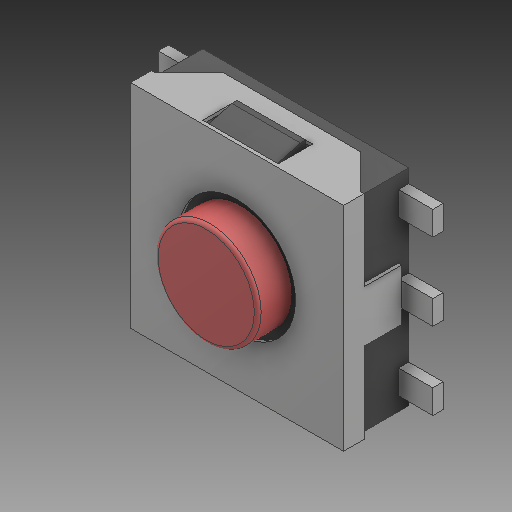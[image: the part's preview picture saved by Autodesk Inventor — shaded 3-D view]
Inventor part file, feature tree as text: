
AUTODESK INVENTOR PART (.ipt)
format: ipt  version: 2020 (Build 240168000, 168)  size: 180,224 bytes
history: native  units: mm
features: other x1, fillet x1
ambient origin geometry x8: Origin, YZ Plane, XZ Plane, XY Plane, X Axis, Y Axis, Z Axis, Center Point
bodies: Body1 (feature_tree)
feature tree (2):
  other  "Твердое тело1"
  fillet  "Fillet1"  [1 undecoded]
note: 1 required parameter value undecoded (feature->parameter linkage not recoverable at this tier; creation-order binding heuristic only, values carry confidence <= 0.55)
